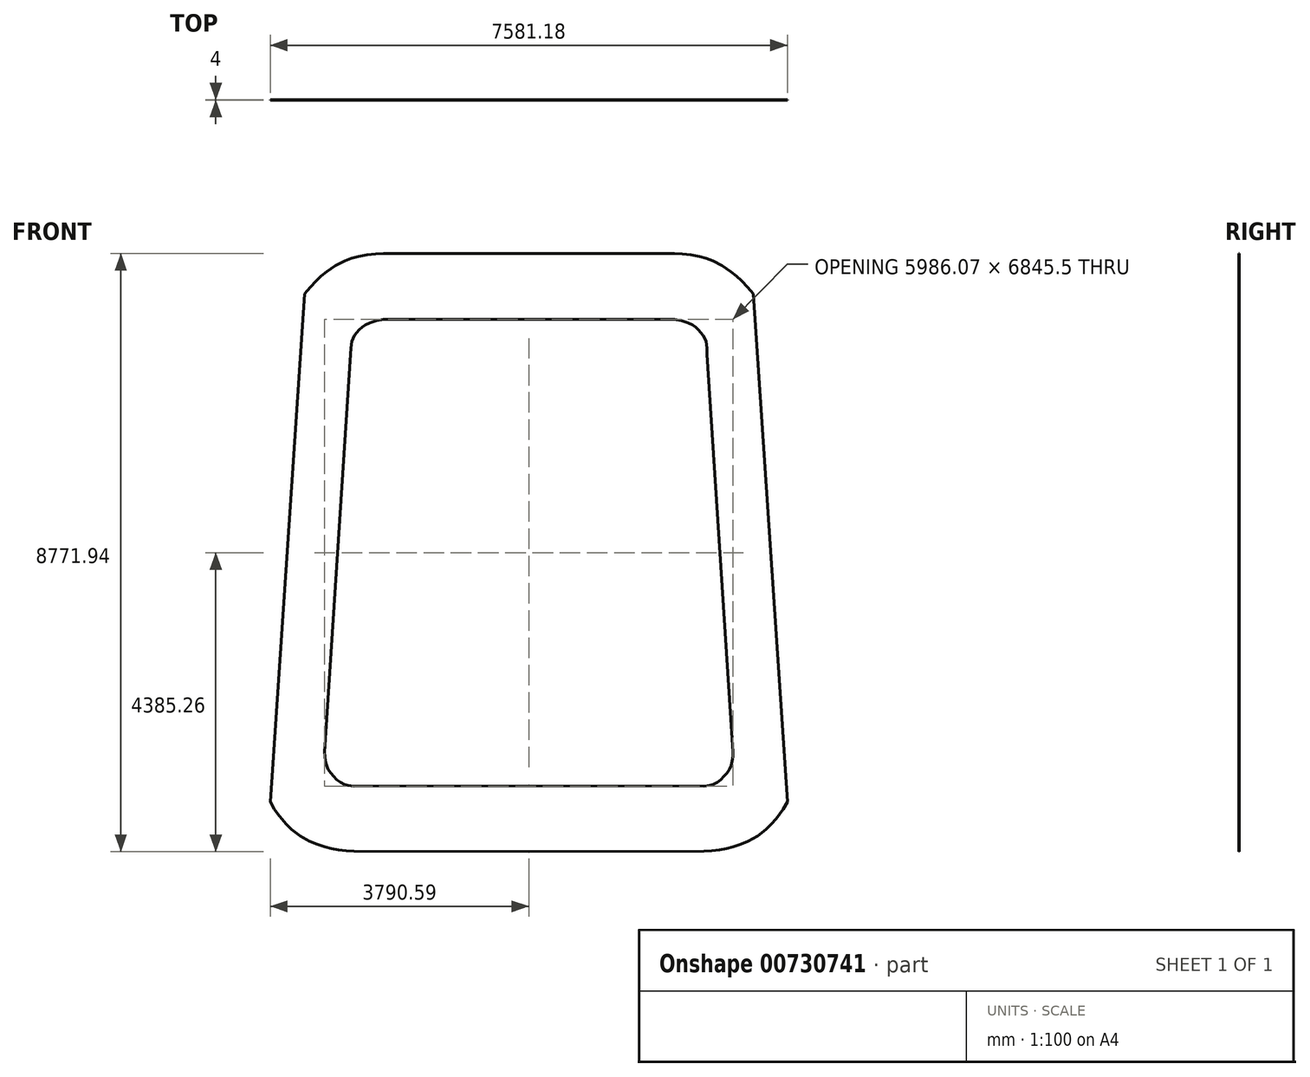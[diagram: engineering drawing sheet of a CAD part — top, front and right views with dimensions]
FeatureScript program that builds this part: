
annotation { "Feature Type Name" : "Feature", "Feature Type Description" : "" }
export const myFeature = defineFeature(function(context is Context, id is Id, definition is map)
    precondition{}
    {
        {
            var Q0;
            Q0=qCreatedBy(makeId("Front.planeOp"),FACE);
            var sketch = newSketch(context, id + "F0", { "sketchPlane" : qUnion([Q0])});
            skLineSegment(sketch, "E0", {"start": v(-3290.32, 3797.1) * mm, "end": v(-3163.6, 3788.59) * mm});
            skLineSegment(sketch, "E1", {"start": v(-3163.6, 3788.59) * mm, "end": v(-3290.32, 3797.1) * mm});
            skLineSegment(sketch, "E2", {"start": v(-3290.32, 3797.1) * mm, "end": v(-3207.61, 3893.1) * mm});
            skLineSegment(sketch, "E3", {"start": v(-3207.61, 3893.1) * mm, "end": v(-3119.25, 3984.04) * mm});
            skLineSegment(sketch, "E4", {"start": v(-3119.25, 3984.04) * mm, "end": v(-3043.33, 4054.2) * mm});
            skLineSegment(sketch, "E5", {"start": v(-3043.33, 4054.2) * mm, "end": v(-2963.4, 4119.8) * mm});
            skLineSegment(sketch, "E6", {"start": v(-2963.4, 4119.8) * mm, "end": v(-2835.66, 4206.82) * mm});
            skLineSegment(sketch, "E7", {"start": v(-2835.66, 4206.82) * mm, "end": v(-2698.45, 4277.9) * mm});
            skLineSegment(sketch, "E8", {"start": v(-2698.45, 4277.9) * mm, "end": v(-2601.01, 4315.33) * mm});
            skLineSegment(sketch, "E9", {"start": v(-2601.01, 4315.33) * mm, "end": v(-2500.63, 4343.65) * mm});
            skLineSegment(sketch, "E10", {"start": v(-2500.63, 4343.65) * mm, "end": v(-2374.95, 4366.31) * mm});
            skLineSegment(sketch, "E11", {"start": v(-2374.95, 4366.31) * mm, "end": v(-2247.75, 4379.47) * mm});
            skLineSegment(sketch, "E12", {"start": v(-2247.75, 4379.47) * mm, "end": v(-2133.57, 4385.97) * mm});
            skLineSegment(sketch, "E13", {"start": v(-2133.57, 4385.97) * mm, "end": v(-2126.36, 4259.17) * mm});
            skLineSegment(sketch, "E14", {"start": v(-2126.36, 4259.17) * mm, "end": v(-2133.57, 4385.97) * mm});
            skLineSegment(sketch, "E15", {"start": v(-2133.57, 4385.97) * mm, "end": v(0, 4384.32) * mm});
            skLineSegment(sketch, "E16", {"start": v(0, 4384.32) * mm, "end": v(-0.1, 4257.32) * mm});
            skLineSegment(sketch, "E17", {"start": v(-0.1, 4257.32) * mm, "end": v(0, 4384.32) * mm});
            skLineSegment(sketch, "E18", {"start": v(0, 4384.32) * mm, "end": v(2133.57, 4385.97) * mm});
            skLineSegment(sketch, "E19", {"start": v(2133.57, 4385.97) * mm, "end": v(2133.68, 4258.97) * mm});
            skLineSegment(sketch, "E20", {"start": v(2133.68, 4258.97) * mm, "end": v(2133.57, 4385.97) * mm});
            skLineSegment(sketch, "E21", {"start": v(2133.57, 4385.97) * mm, "end": v(2247.75, 4379.47) * mm});
            skLineSegment(sketch, "E22", {"start": v(2247.75, 4379.47) * mm, "end": v(2374.95, 4366.31) * mm});
            skLineSegment(sketch, "E23", {"start": v(2374.95, 4366.31) * mm, "end": v(2500.63, 4343.65) * mm});
            skLineSegment(sketch, "E24", {"start": v(2500.63, 4343.65) * mm, "end": v(2601.01, 4315.33) * mm});
            skLineSegment(sketch, "E25", {"start": v(2601.01, 4315.33) * mm, "end": v(2698.45, 4277.9) * mm});
            skLineSegment(sketch, "E26", {"start": v(2698.45, 4277.9) * mm, "end": v(2835.66, 4206.82) * mm});
            skLineSegment(sketch, "E27", {"start": v(2835.66, 4206.82) * mm, "end": v(2963.4, 4119.8) * mm});
            skLineSegment(sketch, "E28", {"start": v(2963.4, 4119.8) * mm, "end": v(3043.33, 4054.2) * mm});
            skLineSegment(sketch, "E29", {"start": v(3043.33, 4054.2) * mm, "end": v(3119.25, 3984.04) * mm});
            skLineSegment(sketch, "E30", {"start": v(3119.25, 3984.04) * mm, "end": v(3207.64, 3893.1) * mm});
            skLineSegment(sketch, "E31", {"start": v(3207.64, 3893.1) * mm, "end": v(3290.32, 3797.1) * mm});
            skLineSegment(sketch, "E32", {"start": v(3290.32, 3797.1) * mm, "end": v(3194.1, 3714.22) * mm});
            skLineSegment(sketch, "E33", {"start": v(3194.1, 3714.22) * mm, "end": v(3290.32, 3797.1) * mm});
            skLineSegment(sketch, "E34", {"start": v(3290.32, 3797.1) * mm, "end": v(3790.6, -3651.86) * mm});
            skLineSegment(sketch, "E35", {"start": v(3790.6, -3651.86) * mm, "end": v(3663.9, -3660.37) * mm});
            skLineSegment(sketch, "E36", {"start": v(3663.9, -3660.37) * mm, "end": v(3790.6, -3651.86) * mm});
            skLineSegment(sketch, "E37", {"start": v(3790.6, -3651.86) * mm, "end": v(3731.51, -3758.16) * mm});
            skLineSegment(sketch, "E38", {"start": v(3731.51, -3758.16) * mm, "end": v(3681.45, -3830.04) * mm});
            skLineSegment(sketch, "E39", {"start": v(3681.45, -3830.04) * mm, "end": v(3626.9, -3898.75) * mm});
            skLineSegment(sketch, "E40", {"start": v(3626.9, -3898.75) * mm, "end": v(3554.15, -3981.88) * mm});
            skLineSegment(sketch, "E41", {"start": v(3554.15, -3981.88) * mm, "end": v(3475.46, -4059.1) * mm});
            skLineSegment(sketch, "E42", {"start": v(3475.46, -4059.1) * mm, "end": v(3351.91, -4153.33) * mm});
            skLineSegment(sketch, "E43", {"start": v(3351.91, -4153.33) * mm, "end": v(3216.17, -4229.38) * mm});
            skLineSegment(sketch, "E44", {"start": v(3216.17, -4229.38) * mm, "end": v(3105.63, -4275.73) * mm});
            skLineSegment(sketch, "E45", {"start": v(3105.63, -4275.73) * mm, "end": v(2991.84, -4313.53) * mm});
            skLineSegment(sketch, "E46", {"start": v(2991.84, -4313.53) * mm, "end": v(2894.1, -4340.02) * mm});
            skLineSegment(sketch, "E47", {"start": v(2894.1, -4340.02) * mm, "end": v(2794.91, -4360.01) * mm});
            skLineSegment(sketch, "E48", {"start": v(2794.91, -4360.01) * mm, "end": v(2680.49, -4372.58) * mm});
            skLineSegment(sketch, "E49", {"start": v(2680.49, -4372.58) * mm, "end": v(2565.37, -4374.77) * mm});
            skLineSegment(sketch, "E50", {"start": v(2565.37, -4374.77) * mm, "end": v(2562.99, -4247.8) * mm});
            skLineSegment(sketch, "E51", {"start": v(2562.99, -4247.8) * mm, "end": v(2565.37, -4374.77) * mm});
            skLineSegment(sketch, "E52", {"start": v(2565.37, -4374.77) * mm, "end": v(0, -4385.97) * mm});
            skLineSegment(sketch, "E53", {"start": v(0, -4385.97) * mm, "end": v(-0.56, -4258.97) * mm});
            skLineSegment(sketch, "E54", {"start": v(-0.56, -4258.97) * mm, "end": v(0, -4385.97) * mm});
            skLineSegment(sketch, "E55", {"start": v(0, -4385.97) * mm, "end": v(-2565.37, -4374.77) * mm});
            skLineSegment(sketch, "E56", {"start": v(-2565.37, -4374.77) * mm, "end": v(-2564.82, -4247.77) * mm});
            skLineSegment(sketch, "E57", {"start": v(-2564.82, -4247.77) * mm, "end": v(-2565.37, -4374.77) * mm});
            skLineSegment(sketch, "E58", {"start": v(-2565.37, -4374.77) * mm, "end": v(-2680.46, -4372.58) * mm});
            skLineSegment(sketch, "E59", {"start": v(-2680.46, -4372.58) * mm, "end": v(-2794.91, -4360.01) * mm});
            skLineSegment(sketch, "E60", {"start": v(-2794.91, -4360.01) * mm, "end": v(-2894.1, -4340.02) * mm});
            skLineSegment(sketch, "E61", {"start": v(-2894.1, -4340.02) * mm, "end": v(-2991.84, -4313.53) * mm});
            skLineSegment(sketch, "E62", {"start": v(-2991.84, -4313.53) * mm, "end": v(-3105.63, -4275.73) * mm});
            skLineSegment(sketch, "E63", {"start": v(-3105.63, -4275.73) * mm, "end": v(-3216.17, -4229.38) * mm});
            skLineSegment(sketch, "E64", {"start": v(-3216.17, -4229.38) * mm, "end": v(-3351.91, -4153.33) * mm});
            skLineSegment(sketch, "E65", {"start": v(-3351.91, -4153.33) * mm, "end": v(-3475.43, -4059.1) * mm});
            skLineSegment(sketch, "E66", {"start": v(-3475.43, -4059.1) * mm, "end": v(-3554.15, -3981.88) * mm});
            skLineSegment(sketch, "E67", {"start": v(-3554.15, -3981.88) * mm, "end": v(-3626.9, -3898.75) * mm});
            skLineSegment(sketch, "E68", {"start": v(-3626.9, -3898.75) * mm, "end": v(-3681.45, -3830.04) * mm});
            skLineSegment(sketch, "E69", {"start": v(-3681.45, -3830.04) * mm, "end": v(-3731.49, -3758.16) * mm});
            skLineSegment(sketch, "E70", {"start": v(-3731.49, -3758.16) * mm, "end": v(-3790.6, -3651.86) * mm});
            skLineSegment(sketch, "E71", {"start": v(-3790.6, -3651.86) * mm, "end": v(-3679.6, -3590.14) * mm});
            skLineSegment(sketch, "E72", {"start": v(-3679.6, -3590.14) * mm, "end": v(-3790.6, -3651.86) * mm});
            skLineSegment(sketch, "E73", {"start": v(-3790.6, -3651.86) * mm, "end": v(-3290.32, 3797.1) * mm});
            skLineSegment(sketch, "E74", {"start": v(0, 3422.04) * mm, "end": v(0.18, 3295.04) * mm});
            skLineSegment(sketch, "E75", {"start": v(0.18, 3295.04) * mm, "end": v(0, 3422.04) * mm});
            skLineSegment(sketch, "E76", {"start": v(0, 3422.04) * mm, "end": v(2133.57, 3419.14) * mm});
            skLineSegment(sketch, "E77", {"start": v(2133.57, 3419.14) * mm, "end": v(2133.42, 3292.14) * mm});
            skLineSegment(sketch, "E78", {"start": v(2133.42, 3292.14) * mm, "end": v(2133.57, 3419.14) * mm});
            skLineSegment(sketch, "E79", {"start": v(2133.57, 3419.14) * mm, "end": v(2234.29, 3403.24) * mm});
            skLineSegment(sketch, "E80", {"start": v(2234.29, 3403.24) * mm, "end": v(2331.85, 3372.54) * mm});
            skLineSegment(sketch, "E81", {"start": v(2331.85, 3372.54) * mm, "end": v(2399.97, 3339.67) * mm});
            skLineSegment(sketch, "E82", {"start": v(2399.97, 3339.67) * mm, "end": v(2445.74, 3306.24) * mm});
            skLineSegment(sketch, "E83", {"start": v(2445.74, 3306.24) * mm, "end": v(2487.32, 3267.2) * mm});
            skLineSegment(sketch, "E84", {"start": v(2487.32, 3267.2) * mm, "end": v(2554.5, 3186.07) * mm});
            skLineSegment(sketch, "E85", {"start": v(2554.5, 3186.07) * mm, "end": v(2579.01, 3143.45) * mm});
            skLineSegment(sketch, "E86", {"start": v(2579.01, 3143.45) * mm, "end": v(2596.64, 3097.8) * mm});
            skLineSegment(sketch, "E87", {"start": v(2596.64, 3097.8) * mm, "end": v(2610.49, 3004.29) * mm});
            skLineSegment(sketch, "E88", {"start": v(2610.49, 3004.29) * mm, "end": v(2613.79, 2904.26) * mm});
            skLineSegment(sketch, "E89", {"start": v(2613.79, 2904.26) * mm, "end": v(2486.86, 2900.05) * mm});
            skLineSegment(sketch, "E90", {"start": v(2486.86, 2900.05) * mm, "end": v(2613.79, 2904.26) * mm});
            skLineSegment(sketch, "E91", {"start": v(2613.79, 2904.26) * mm, "end": v(2993.03, -2922.02) * mm});
            skLineSegment(sketch, "E92", {"start": v(2993.03, -2922.02) * mm, "end": v(2866.31, -2930.27) * mm});
            skLineSegment(sketch, "E93", {"start": v(2866.31, -2930.27) * mm, "end": v(2993.03, -2922.02) * mm});
            skLineSegment(sketch, "E94", {"start": v(2993.03, -2922.02) * mm, "end": v(2991.84, -2988.16) * mm});
            skLineSegment(sketch, "E95", {"start": v(2991.84, -2988.16) * mm, "end": v(2982.77, -3053.64) * mm});
            skLineSegment(sketch, "E96", {"start": v(2982.77, -3053.64) * mm, "end": v(2965.83, -3118.26) * mm});
            skLineSegment(sketch, "E97", {"start": v(2965.83, -3118.26) * mm, "end": v(2942.82, -3177.24) * mm});
            skLineSegment(sketch, "E98", {"start": v(2942.82, -3177.24) * mm, "end": v(2903.1, -3232.5) * mm});
            skLineSegment(sketch, "E99", {"start": v(2903.1, -3232.5) * mm, "end": v(2861.06, -3280.92) * mm});
            skLineSegment(sketch, "E100", {"start": v(2861.06, -3280.92) * mm, "end": v(2815.16, -3328.77) * mm});
            skLineSegment(sketch, "E101", {"start": v(2815.16, -3328.77) * mm, "end": v(2763.19, -3367.81) * mm});
            skLineSegment(sketch, "E102", {"start": v(2763.19, -3367.81) * mm, "end": v(2702.84, -3397.25) * mm});
            skLineSegment(sketch, "E103", {"start": v(2702.84, -3397.25) * mm, "end": v(2651.58, -3412.44) * mm});
            skLineSegment(sketch, "E104", {"start": v(2651.58, -3412.44) * mm, "end": v(2565.37, -3423.46) * mm});
            skLineSegment(sketch, "E105", {"start": v(2565.37, -3423.46) * mm, "end": v(2549.27, -3297.5) * mm});
            skLineSegment(sketch, "E106", {"start": v(2549.27, -3297.5) * mm, "end": v(2565.37, -3423.46) * mm});
            skLineSegment(sketch, "E107", {"start": v(2565.37, -3423.46) * mm, "end": v(0, -3418) * mm});
            skLineSegment(sketch, "E108", {"start": v(0, -3418) * mm, "end": v(0.28, -3291) * mm});
            skLineSegment(sketch, "E109", {"start": v(0.28, -3291) * mm, "end": v(0, -3418) * mm});
            skLineSegment(sketch, "E110", {"start": v(0, -3418) * mm, "end": v(-2565.37, -3423.46) * mm});
            skLineSegment(sketch, "E111", {"start": v(-2565.37, -3423.46) * mm, "end": v(-2565.65, -3296.46) * mm});
            skLineSegment(sketch, "E112", {"start": v(-2565.65, -3296.46) * mm, "end": v(-2565.37, -3423.46) * mm});
            skLineSegment(sketch, "E113", {"start": v(-2565.37, -3423.46) * mm, "end": v(-2651.58, -3412.44) * mm});
            skLineSegment(sketch, "E114", {"start": v(-2651.58, -3412.44) * mm, "end": v(-2702.84, -3397.25) * mm});
            skLineSegment(sketch, "E115", {"start": v(-2702.84, -3397.25) * mm, "end": v(-2763.19, -3367.81) * mm});
            skLineSegment(sketch, "E116", {"start": v(-2763.19, -3367.81) * mm, "end": v(-2815.16, -3328.77) * mm});
            skLineSegment(sketch, "E117", {"start": v(-2815.16, -3328.77) * mm, "end": v(-2861.06, -3280.92) * mm});
            skLineSegment(sketch, "E118", {"start": v(-2861.06, -3280.92) * mm, "end": v(-2903.1, -3232.5) * mm});
            skLineSegment(sketch, "E119", {"start": v(-2903.1, -3232.5) * mm, "end": v(-2942.82, -3177.24) * mm});
            skLineSegment(sketch, "E120", {"start": v(-2942.82, -3177.24) * mm, "end": v(-2965.83, -3118.26) * mm});
            skLineSegment(sketch, "E121", {"start": v(-2965.83, -3118.26) * mm, "end": v(-2982.77, -3053.64) * mm});
            skLineSegment(sketch, "E122", {"start": v(-2982.77, -3053.64) * mm, "end": v(-2991.84, -2988.16) * mm});
            skLineSegment(sketch, "E123", {"start": v(-2991.84, -2988.16) * mm, "end": v(-2993.03, -2922.02) * mm});
            skLineSegment(sketch, "E124", {"start": v(-2993.03, -2922.02) * mm, "end": v(-2866.06, -2919.7) * mm});
            skLineSegment(sketch, "E125", {"start": v(-2866.06, -2919.7) * mm, "end": v(-2993.03, -2922.02) * mm});
            skLineSegment(sketch, "E126", {"start": v(-2993.03, -2922.02) * mm, "end": v(-2613.79, 2904.26) * mm});
            skLineSegment(sketch, "E127", {"start": v(-2613.79, 2904.26) * mm, "end": v(-2610.46, 3004.29) * mm});
            skLineSegment(sketch, "E128", {"start": v(-2610.46, 3004.29) * mm, "end": v(-2596.64, 3097.8) * mm});
            skLineSegment(sketch, "E129", {"start": v(-2596.64, 3097.8) * mm, "end": v(-2578.99, 3143.45) * mm});
            skLineSegment(sketch, "E130", {"start": v(-2578.99, 3143.45) * mm, "end": v(-2554.48, 3186.07) * mm});
            skLineSegment(sketch, "E131", {"start": v(-2554.48, 3186.07) * mm, "end": v(-2487.3, 3267.2) * mm});
            skLineSegment(sketch, "E132", {"start": v(-2487.3, 3267.2) * mm, "end": v(-2445.74, 3306.24) * mm});
            skLineSegment(sketch, "E133", {"start": v(-2445.74, 3306.24) * mm, "end": v(-2399.97, 3339.67) * mm});
            skLineSegment(sketch, "E134", {"start": v(-2399.97, 3339.67) * mm, "end": v(-2331.85, 3372.54) * mm});
            skLineSegment(sketch, "E135", {"start": v(-2331.85, 3372.54) * mm, "end": v(-2234.29, 3403.24) * mm});
            skLineSegment(sketch, "E136", {"start": v(-2234.29, 3403.24) * mm, "end": v(-2133.57, 3419.14) * mm});
            skLineSegment(sketch, "E137", {"start": v(-2133.57, 3419.14) * mm, "end": v(-2113.79, 3293.7) * mm});
            skLineSegment(sketch, "E138", {"start": v(-2113.79, 3293.7) * mm, "end": v(-2133.57, 3419.14) * mm});
            skLineSegment(sketch, "E139", {"start": v(-2133.57, 3419.14) * mm, "end": v(0, 3422.04) * mm});
            skSolve(sketch);
        }
        {
            var Q0;
            Q0 = qSketchRegion(id + "F0", true);
            extrude(context, id + "F1", {"entities" : qUnion([Q0]), "depth" : 4 * mm, "offsetDistance" : 25 * mm});
        }
    });
